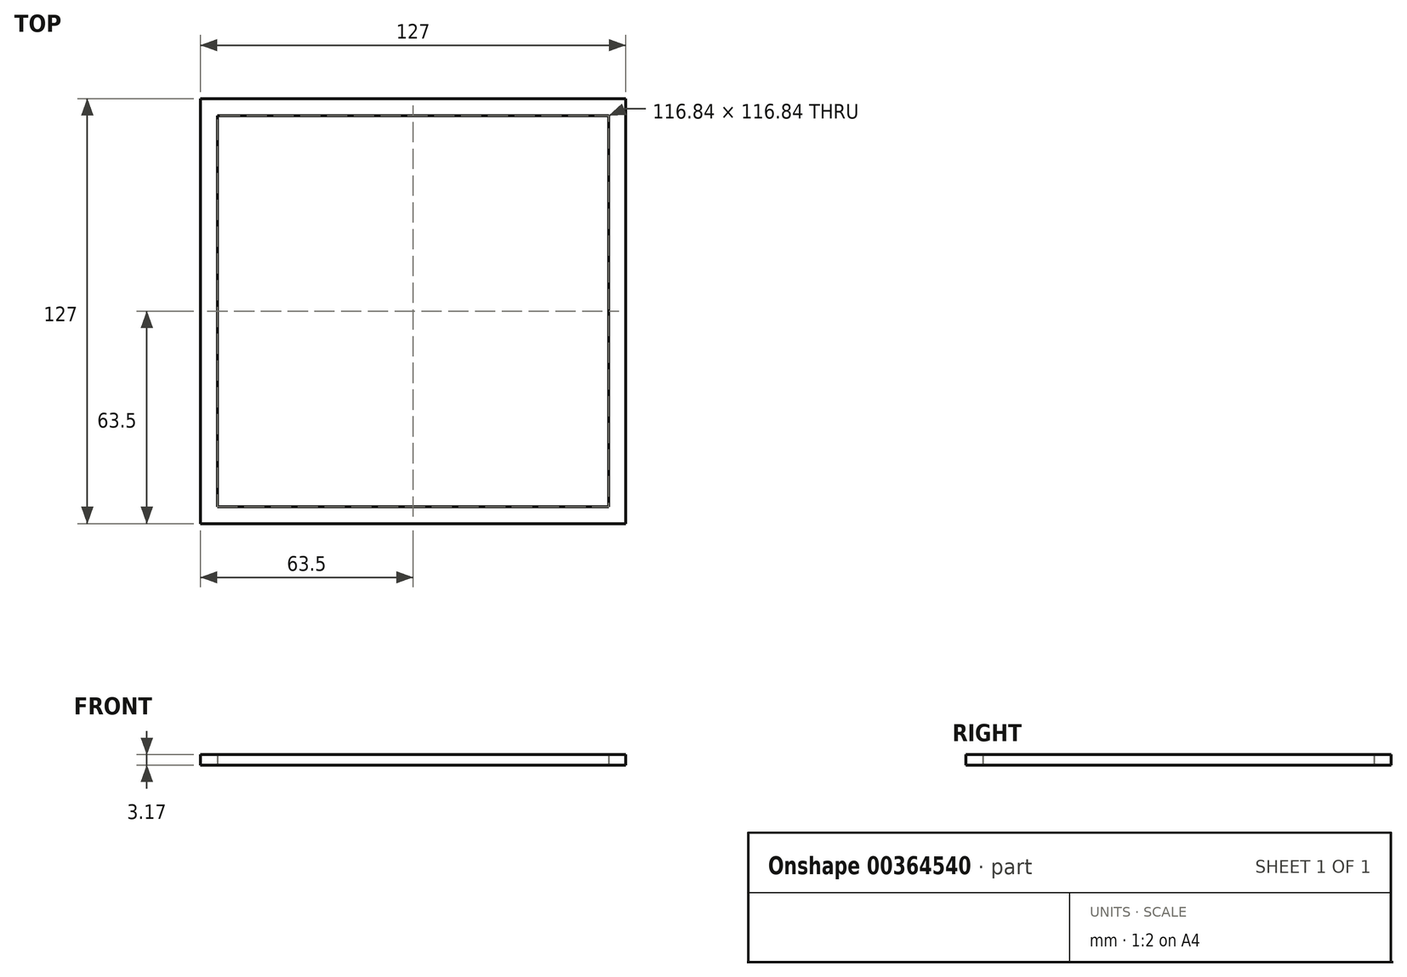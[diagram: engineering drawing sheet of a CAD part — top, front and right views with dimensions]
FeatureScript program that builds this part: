
annotation { "Feature Type Name" : "Feature", "Feature Type Description" : "" }
export const myFeature = defineFeature(function(context is Context, id is Id, definition is map)
    precondition{}
    {
        {
            var Q0;
            Q0=qCreatedBy(makeId("Top.planeOp"),FACE);
            var sketch = newSketch(context, id + "F0", { "sketchPlane" : qUnion([Q0])});
            skLineSegment(sketch, "E0.bottom", {"start": v(-63.5, 63.5) * mm, "end": v(63.5, 63.5) * mm});
            skLineSegment(sketch, "E0.top", {"start": v(-63.5, -63.5) * mm, "end": v(63.5, -63.5) * mm});
            skLineSegment(sketch, "E0.left", {"start": v(-63.5, 63.5) * mm, "end": v(-63.5, -63.5) * mm});
            skLineSegment(sketch, "E0.right", {"start": v(63.5, 63.5) * mm, "end": v(63.5, -63.5) * mm});
            skLineSegment(sketch, "E1.0", {"start": v(-58.42, 58.42) * mm, "end": v(58.42, 58.42) * mm});
            skLineSegment(sketch, "E1.1", {"start": v(-58.42, 58.42) * mm, "end": v(-58.42, -58.42) * mm});
            skLineSegment(sketch, "E1.2", {"start": v(-58.42, -58.42) * mm, "end": v(58.42, -58.42) * mm});
            skLineSegment(sketch, "E1.3", {"start": v(58.42, 58.42) * mm, "end": v(58.42, -58.42) * mm});
            skSolve(sketch);
        }
        {
            var Q0;
            Q0=makeQuery(id+"F0.imprint","IMPRINT",FACE,{"disambiguationData":[TD([[makeQuery(id+"F0.imprint","IMPRINT",EDGE,{"derivedFrom":sQuery(id+"F0.wireOp",EDGE,"E0.bottom")}),-1.0]])]});
            extrude(context, id + "F1", {"entities" : qUnion([Q0]), "depth" : 3.17 * mm, "offsetDistance" : 25.4 * mm});
        }
    });
